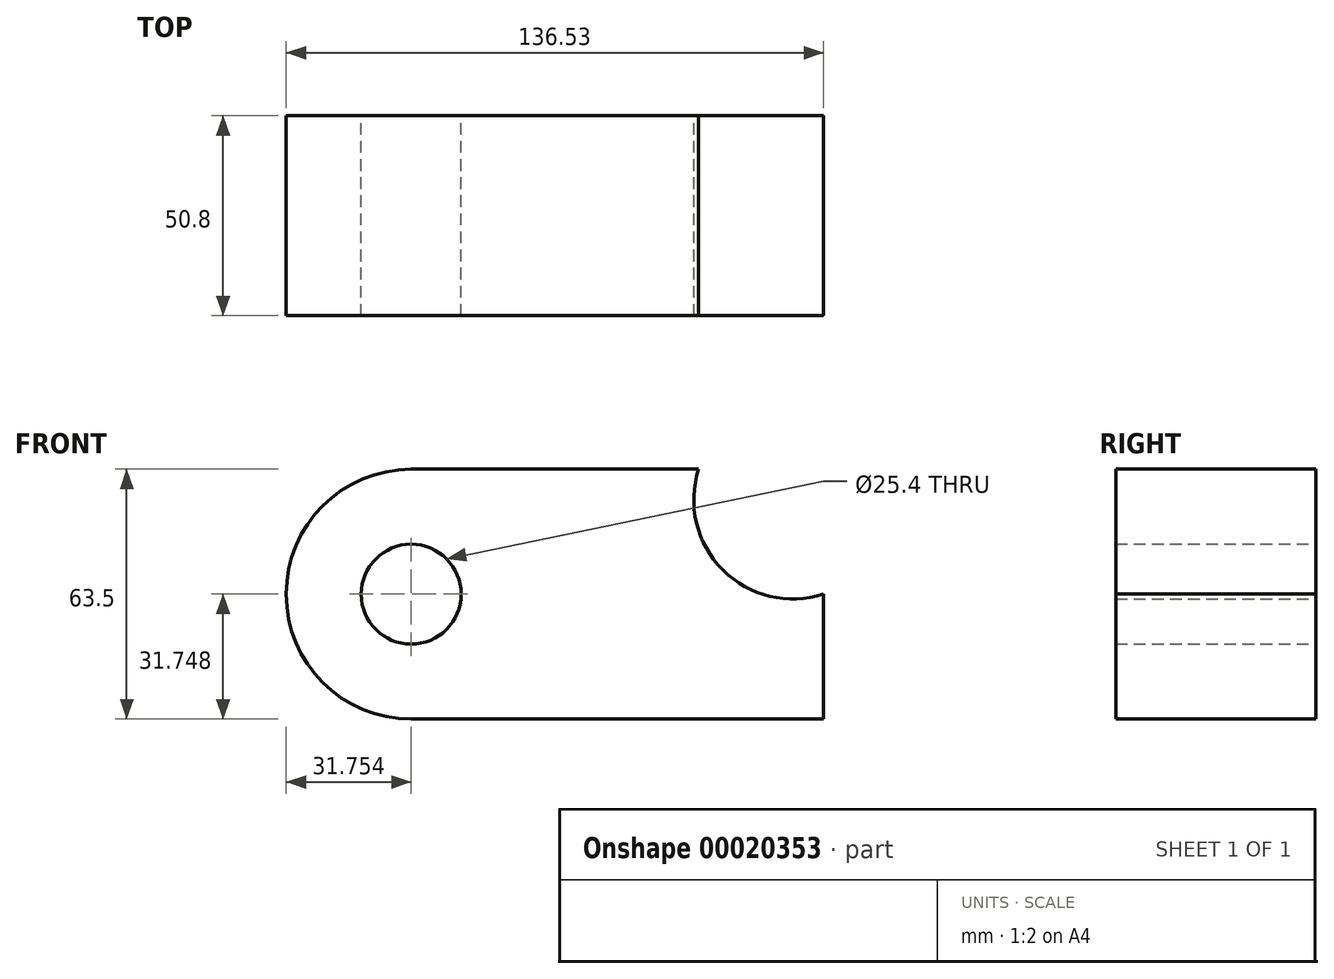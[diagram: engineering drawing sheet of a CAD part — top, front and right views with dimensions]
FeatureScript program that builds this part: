
annotation { "Feature Type Name" : "Feature", "Feature Type Description" : "" }
export const myFeature = defineFeature(function(context is Context, id is Id, definition is map)
    precondition{}
    {
        {
            var Q0;
            Q0=qCreatedBy(makeId("Front.planeOp"),FACE);
            var sketch = newSketch(context, id + "F0", { "sketchPlane" : qUnion([Q0])});
            skLineSegment(sketch, "E0", {"start": v(-28.3, 30.56) * mm, "end": v(44.73, 30.56) * mm});
            skLineSegment(sketch, "E1", {"start": v(76.48, -1.2) * mm, "end": v(76.48, -32.94) * mm});
            skLineSegment(sketch, "E2", {"start": v(-28.3, -32.94) * mm, "end": v(76.48, -32.94) * mm});
            skCircle(sketch, "E3", {"center": v(-28.3, -1.2) * mm, "radius": 12.7 * mm});
            skArc(sketch, "E4", {"start": v(-28.3, 30.56) * mm, "mid": v(-60.05, -1.2) * mm, "end": v(-28.3, -32.94) * mm});
            skPoint(sketch, "E5.orphan", {"position": v(-60.05, -1.2) * mm});
            skLineSegment(sketch, "E6", {"start": v(44.73, 30.56) * mm, "end": v(76.48, 30.56) * mm});
            skLineSegment(sketch, "E7", {"start": v(76.48, 30.56) * mm, "end": v(76.48, -1.2) * mm});
            skArc(sketch, "E8", {"start": v(44.73, 30.56) * mm, "mid": v(50.88, 4.96) * mm, "end": v(76.48, -1.2) * mm});
            skSolve(sketch);
        }
        {
            var Q0;
            Q0=makeQuery(id+"F0.imprint","IMPRINT",FACE,{"disambiguationData":[TD([[makeQuery(id+"F0.imprint","IMPRINT",EDGE,{"derivedFrom":sQuery(id+"F0.wireOp",EDGE,"E0")}),-1.0]])]});
            extrude(context, id + "F1", {"entities" : qUnion([Q0]), "depth" : 50.8 * mm});
        }
    });
